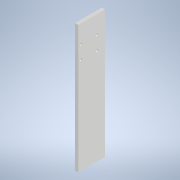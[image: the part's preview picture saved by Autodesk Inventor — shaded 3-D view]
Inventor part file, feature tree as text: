
AUTODESK INVENTOR PART (.ipt)
format: ipt  version: 2022 (Build 260153000, 153)  size: 118,272 bytes
history: native  units: mm
features: sketch x2, other x1, extrude x1, hole x1
ambient origin geometry x8: Origin, YZ Plane, XZ Plane, XY Plane, X Axis, Y Axis, Z Axis, Center Point
bodies: Body1 (feature_tree)
feature tree (5):
  other  "ソリッド1"
  extrude  "押し出し1"  Depth=40.0mm
  hole  "穴1"  [1 undecoded]
  sketch  "スケッチ1"
  sketch  "スケッチ2"
note: 1 required parameter value undecoded (feature->parameter linkage not recoverable at this tier; creation-order binding heuristic only, values carry confidence <= 0.55)
